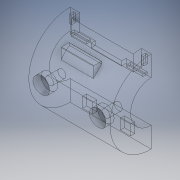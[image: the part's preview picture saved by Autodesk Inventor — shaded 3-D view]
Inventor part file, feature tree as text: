
AUTODESK INVENTOR PART (.ipt)
format: ipt  version: 2018 (Build 220112000, 112)  size: 260,096 bytes
history: native  units: in
note: dims shown in document units (in); Inventor stores cm internally (conversion verified against a paired STEP export)
features: extrude x9, sketch x8, plane x2, fillet x1
ambient origin geometry x8: Origin, YZ Plane, XZ Plane, XY Plane, X Axis, Y Axis, Z Axis, Center Point
bodies: Solid1 (feature_tree)
feature tree (20):
  extrude  "Extrusion1"  Depth=1.0in
  plane  "Work Plane1"
  extrude  "Extrusion2"  Depth=0.5in
  extrude  "Extrusion3"  TaperAngle=180.0deg  [1 undecoded]
  plane  "Work Plane2"
  extrude  "Extrusion5"  Depth=1.9685in TaperAngle=0.0deg
  extrude  "Extrusion6"  Depth=0.3in
  extrude  "Extrusion8"  Depth=0.4in
  extrude  "Extrusion10"  Depth=0.6843in
  extrude  "Extrusion11"  Depth=0.01in
  extrude  "Extrusion12"  Depth=0.01in
  fillet  "Fillet5"  Radius=0.19in
  sketch  "Sketch2"  dims[d0=1.0in d1=0.5in]
  sketch  "Sketch3"  dims[d2=0.5in d3=0.5in]
  sketch  "Sketch4"  dims[d4=0.0in d5=180.0deg]
  sketch  "Sketch7"  dims[d6=0.0in d7=1.9685in d8=0.0in]
  sketch  "Sketch8"  dims[d9=0.3in d10=0.3in]
  sketch  "Sketch10"  dims[d11=0.4in d12=0.4in]
  sketch  "Sketch14"  dims[d15=0.2in d16=0.0in d17=0.3in d18=0.3in d20=0.19in d21=0.19in d22=0.6843in d23=0.6843in d24=1.0in d25=0.0in d33=1.5in d34=0.4in d35=0.4in d36=0.0in d37=0.75in d38=0.2in d39=0.4in d40=0.0in d50=0.1in d51=0.1in d52=0.4in d53=0.4in d54=0.05in d56=0.1in d57=0.0in d58=0.025in d59=0.05in d60=0.0092in d74=0.09in d75=0.05in d76=0.05in d77=0.2in d78=0.05in d79=0.2in d80=0.09in d81=0.25in d82=0.1in d83=0.0in d97=0.7874in d98=0.0in d104=0.4in d105=0.4in d106=0.25in d107=0.25in d108=0.125in d109=0.25in d110=0.25in d111=0.1in d112=0.0in d114=45.0deg d115=0.2in d116=0.1in d117=0.3in d118=0.15in d119=0.01in]
  sketch  "Sketch13"  dims[d13=0.6843in d14=0.6843in]
note: 1 required parameter value undecoded (feature->parameter linkage not recoverable at this tier; creation-order binding heuristic only, values carry confidence <= 0.55)
